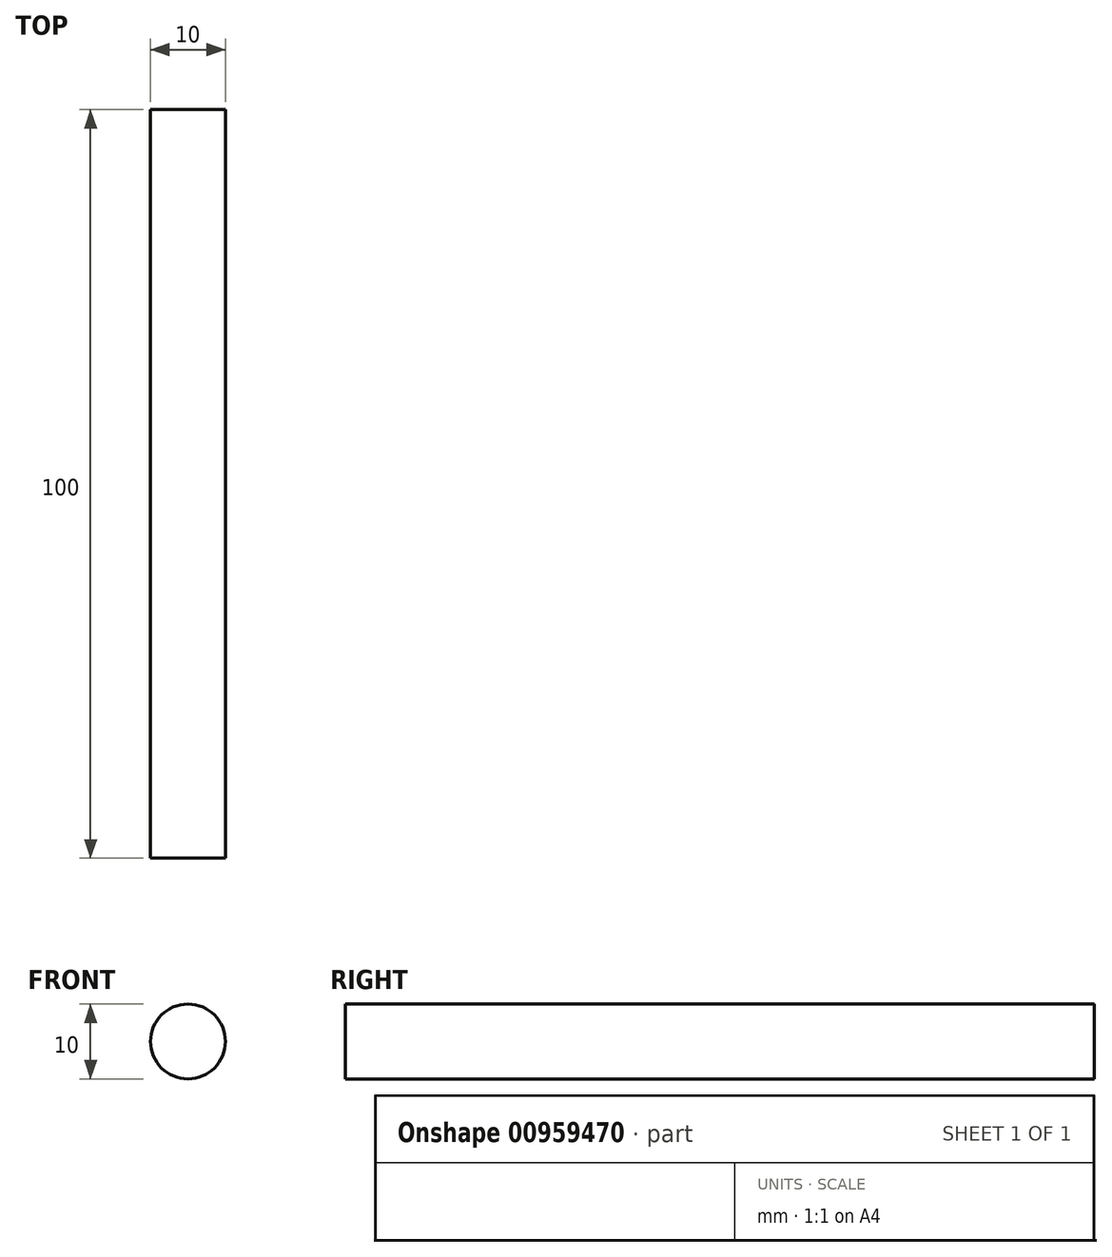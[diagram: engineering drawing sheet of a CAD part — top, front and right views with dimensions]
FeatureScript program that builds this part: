
annotation { "Feature Type Name" : "Feature", "Feature Type Description" : "" }
export const myFeature = defineFeature(function(context is Context, id is Id, definition is map)
    precondition{}
    {
        {
            var Q0;
            Q0=qCreatedBy(makeId("Front.planeOp"),FACE);
            var sketch = newSketch(context, id + "F0", { "sketchPlane" : qUnion([Q0])});
            skCircle(sketch, "E0", {"center": v(0, 0) * mm, "radius": 5 * mm});
            skSolve(sketch);
        }
        {
            var Q0;
            Q0=makeQuery(id+"F0.imprint","IMPRINT",FACE,{"disambiguationData":[TD([[makeQuery(id+"F0.imprint","IMPRINT",EDGE,{"derivedFrom":sQuery(id+"F0.wireOp",EDGE,"E0")}),1.0]])]});
            extrude(context, id + "F1", {"entities" : qUnion([Q0]), "depth" : 100 * mm, "offsetDistance" : 25 * mm});
        }
    });
